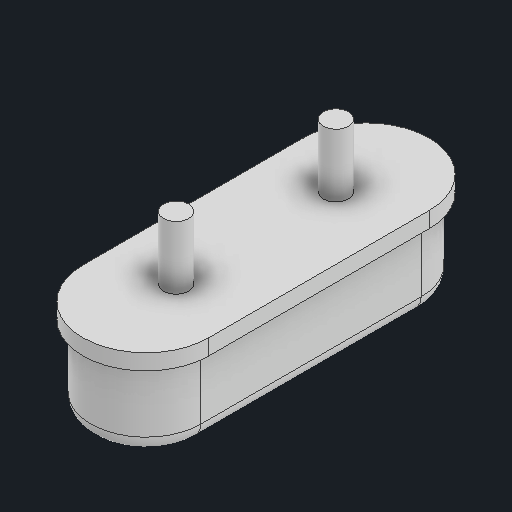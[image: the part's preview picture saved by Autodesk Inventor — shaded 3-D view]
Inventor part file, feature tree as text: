
AUTODESK INVENTOR PART (.ipt)
format: ipt  version: 2023 (Build 270158000, 158)  size: 576,000 bytes
history: native  units: in
note: dims shown in document units (in); Inventor stores cm internally (conversion verified against a paired STEP export)
features: fillet x1
ambient origin geometry x8: Origin, YZ Plane, XZ Plane, XY Plane, X Axis, Y Axis, Z Axis, Center Point
bodies: Solid1 (feature_tree)
feature tree (1):
  fillet  "Fillet2"  [1 undecoded]
note: 1 required parameter value undecoded (feature->parameter linkage not recoverable at this tier; creation-order binding heuristic only, values carry confidence <= 0.55)
